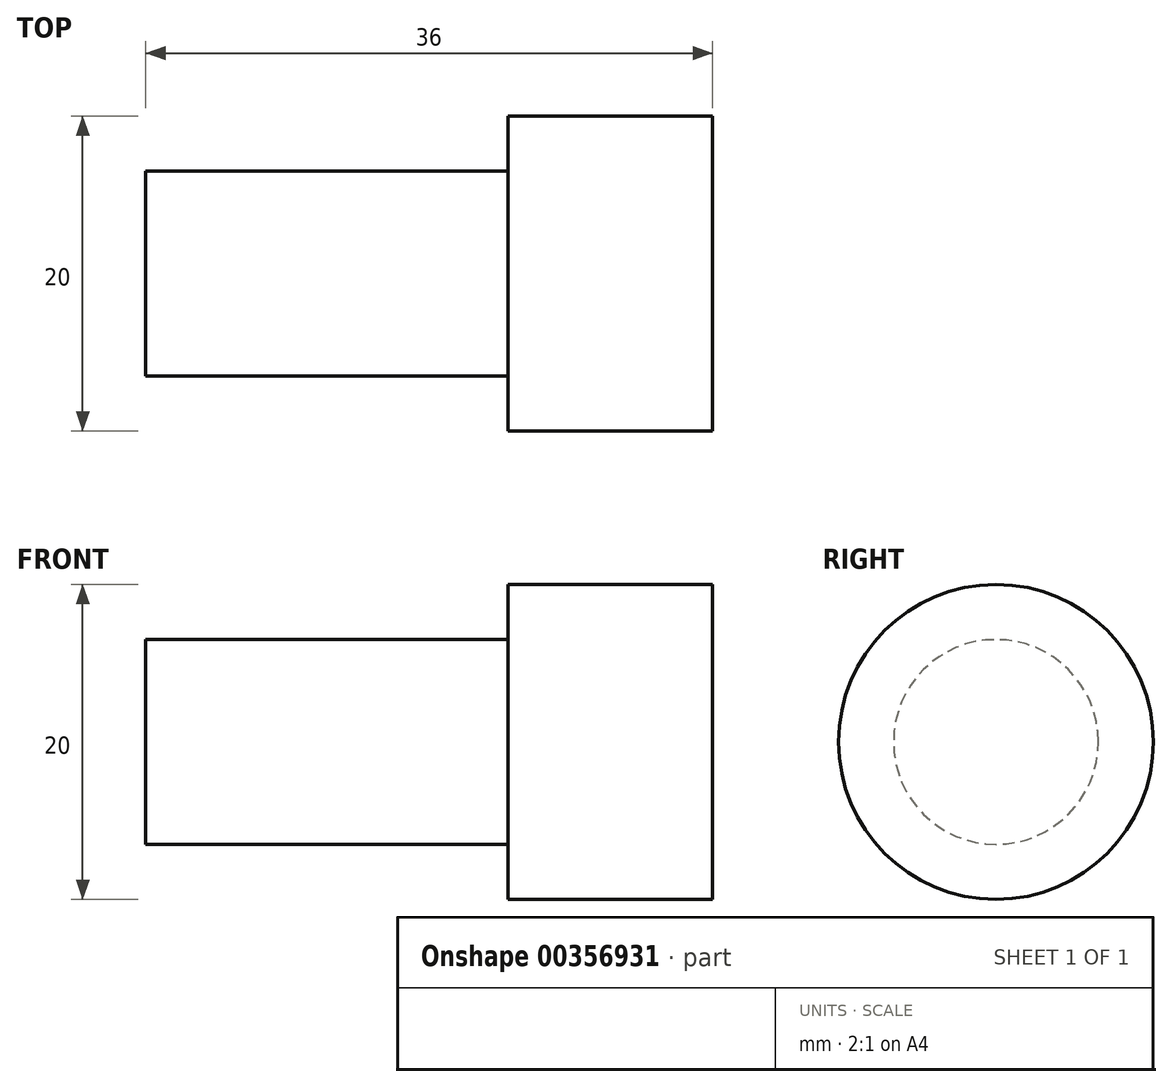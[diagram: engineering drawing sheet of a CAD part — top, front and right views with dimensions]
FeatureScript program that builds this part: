
annotation { "Feature Type Name" : "Feature", "Feature Type Description" : "" }
export const myFeature = defineFeature(function(context is Context, id is Id, definition is map)
    precondition{}
    {
        {
            var Q0;
            Q0=qCreatedBy(makeId("Top.planeOp"),FACE);
            var sketch = newSketch(context, id + "F0", { "sketchPlane" : qUnion([Q0])});
            skLineSegment(sketch, "E0.bottom", {"start": v(-84, 6.5) * mm, "end": v(-61, 6.5) * mm});
            skLineSegment(sketch, "E0.top", {"start": v(-84, -6.5) * mm, "end": v(-61, -6.5) * mm});
            skLineSegment(sketch, "E0.left", {"start": v(-84, 6.5) * mm, "end": v(-84, -6.5) * mm});
            skLineSegment(sketch, "E0.right", {"start": v(-61, 6.5) * mm, "end": v(-61, -6.5) * mm});
            skLineSegment(sketch, "E1.bottom", {"start": v(-61, -10) * mm, "end": v(-48, -10) * mm});
            skLineSegment(sketch, "E1.top", {"start": v(-61, 10) * mm, "end": v(-48, 10) * mm});
            skLineSegment(sketch, "E1.left", {"start": v(-61, -10) * mm, "end": v(-61, 10) * mm});
            skLineSegment(sketch, "E1.right", {"start": v(-48, -10) * mm, "end": v(-48, 10) * mm});
            skArc(sketch, "E2", {"start": v(-22.64, -11.9) * mm, "mid": v(-35.16, -8.77) * mm, "end": v(-48, -10) * mm});
            skArc(sketch, "E3", {"start": v(-22.64, -11.9) * mm, "mid": v(6.13, -16.35) * mm, "end": v(33.24, -5.75) * mm});
            skArc(sketch, "E4", {"start": v(33.24, -5.75) * mm, "mid": v(36.15, 0) * mm, "end": v(33.24, 5.75) * mm});
            skArc(sketch, "E5.MirrorCS", {"start": v(-22.64, 11.9) * mm, "mid": v(6.13, 16.35) * mm, "end": v(33.24, 5.75) * mm});
            skArc(sketch, "E6.MirrorCS", {"start": v(-22.64, 11.9) * mm, "mid": v(-35.16, 8.77) * mm, "end": v(-48, 10) * mm});
            skLineSegment(sketch, "E7", {"start": v(36.15, 0) * mm, "end": v(-84, 0) * mm});
            skSolve(sketch);
        }
        {
            var Q0;
            {var subQ1=sQuery(id+"F0.wireOp",EDGE,"E5.MirrorCS");Q0=makeQuery(id+"F0.imprint","IMPRINT",FACE,{"disambiguationData":[TD([[makeQuery(id+"F0.imprint","IMPRINT",EDGE,{"derivedFrom":subQ1}),-1.0]])]});}
            var Q1;
            {var subQ1=sQuery(id+"F0.wireOp",EDGE,"E1.top");Q1=makeQuery(id+"F0.imprint","IMPRINT",FACE,{"disambiguationData":[TD([[makeQuery(id+"F0.imprint","IMPRINT",EDGE,{"derivedFrom":subQ1}),-1.0]])]});}
            var Q2;
            {var subQ0=sQuery(id+"F0.wireOp",EDGE,"E0.bottom");Q2=makeQuery(id+"F0.imprint","IMPRINT",FACE,{"disambiguationData":[TD([[makeQuery(id+"F0.imprint","IMPRINT",EDGE,{"derivedFrom":subQ0}),-1.0]])]});}
            var Q3;
            Q3=sQuery(id+"F0.wireOp",EDGE,"E7");
            revolve(context, id + "F1", {"entities" : qUnion([Q0, Q1, Q2]), "axis" : qUnion([Q3]), "revolveType" : RevolveType.FULL});
        }
    });
